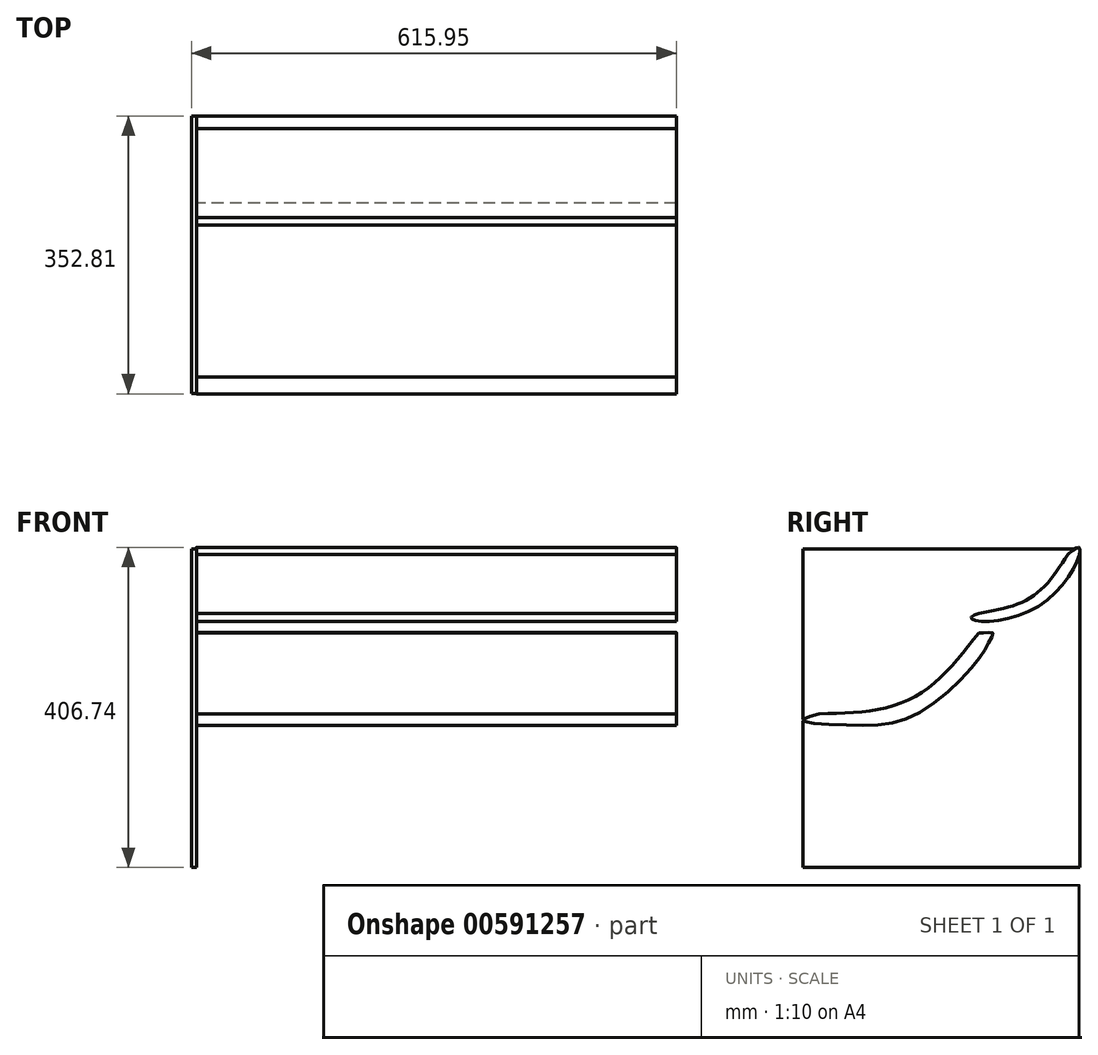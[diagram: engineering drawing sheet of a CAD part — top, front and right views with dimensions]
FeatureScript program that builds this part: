
annotation { "Feature Type Name" : "Feature", "Feature Type Description" : "" }
export const myFeature = defineFeature(function(context is Context, id is Id, definition is map)
    precondition{}
    {
        {
            var Q0;
            Q0=qCreatedBy(makeId("Right.planeOp"),FACE);
            var sketch = newSketch(context, id + "F0", { "sketchPlane" : qUnion([Q0])});
            skFitSpline(sketch, "E0", {"points": [v(0, 0) * mm, v(-84.84, -83.14) * mm, v(-202.69, -102.73) * mm], "startDerivative": vector(-153.6, -199.81) * mm, "endDerivative": vector(-255.31, -2.32) * mm});
            skFitSpline(sketch, "E1", {"points": [v(0, 24.7) * mm, v(68.03, 46.04) * mm, v(113.07, 99.37) * mm], "startDerivative": vector(146.6, 26.15) * mm, "endDerivative": vector(79.4, 123.34) * mm});
            skFitSpline(sketch, "E2", {"points": [v(0, 24.7) * mm, v(-9.7, 19.42) * mm, v(3.34, 14.58) * mm, v(77.95, 35.19) * mm, v(125.93, 93.05) * mm, v(127.35, 108.58) * mm, v(113.07, 99.37) * mm], "startDerivative": vector(-139.52, -51.1) * mm, "endDerivative": vector(-140.04, -121.07) * mm});
            skFitSpline(sketch, "E3", {"points": [v(-202.69, -102.73) * mm, v(-224.08, -110.89) * mm, v(-162.86, -117.17) * mm, v(-77.74, -102.73) * mm, v(0, -33.25) * mm, v(14.44, -9.27) * mm, v(17.97, 0) * mm, v(9.87, 0) * mm, v(0, 0) * mm], "startDerivative": vector(-251.02, -67.67) * mm, "endDerivative": vector(-147.63, 8.82) * mm});
            skSolve(sketch);
        }
        {
            var Q0;
            Q0 = qSketchRegion(id + "F0", true);
            extrude(context, id + "F1", {"entities" : qUnion([Q0]), "depth" : 304.8 * mm, "offsetDistance" : 25.4 * mm, "hasSecondDirection" : true, "secondDirectionOppositeDirection" : true, "secondDirectionDepth" : 304.8 * mm});
        }
        {
            var Q0;
            Q0=makeQuery(id+"F1.opExtrude","CAP_FACE",FACE,{"disambiguationData":[OSD([sQuery(id+"F0.wireOp",EDGE,"E1"),sQuery(id+"F0.wireOp",EDGE,"E2")])],"isStart":true});
            var sketch = newSketch(context, id + "F2", { "sketchPlane" : qUnion([Q0])});
            skLineSegment(sketch, "E4.bottom", {"start": v(-128.55, 106.87) * mm, "end": v(223.46, 106.87) * mm});
            skLineSegment(sketch, "E4.top", {"start": v(-128.55, -298.04) * mm, "end": v(223.46, -298.04) * mm});
            skLineSegment(sketch, "E4.left", {"start": v(-128.55, 106.87) * mm, "end": v(-128.55, -298.04) * mm});
            skLineSegment(sketch, "E4.right", {"start": v(223.46, 106.87) * mm, "end": v(223.46, -298.04) * mm});
            skSolve(sketch);
        }
        {
            var Q0;
            Q0 = qSketchRegion(id + "F2", true);
            extrude(context, id + "F3", {"entities" : qUnion([Q0]), "depth" : 6.35 * mm, "offsetDistance" : 25.4 * mm});
        }
    });
